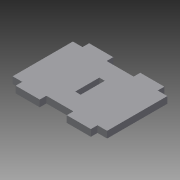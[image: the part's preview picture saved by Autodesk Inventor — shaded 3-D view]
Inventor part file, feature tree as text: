
AUTODESK INVENTOR PART (.ipt)
format: ipt  version: 2015 (Build 190159000, 159)  size: 99,328 bytes
history: native  units: mm
features: extrude x2, sketch x2
ambient origin geometry x8: Origin, YZ Plane, XZ Plane, XY Plane, X Axis, Y Axis, Z Axis, Center Point
bodies: Solid1 (feature_tree)
feature tree (4):
  extrude  "Extrusion1"  Depth=20.0mm
  extrude  "Extrusion2"  Depth=20.0mm
  sketch  "Sketch1"  dims[d2=5.5mm d3=20.0mm]
  sketch  "Sketch2"  dims[d4=5.5mm d5=20.0mm d6=90.0deg d16=5.5mm d17=0.0mm d18=8.0mm d20=8.0mm d23=10.0mm d24=0.0mm]
